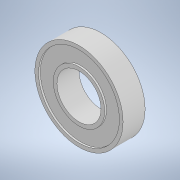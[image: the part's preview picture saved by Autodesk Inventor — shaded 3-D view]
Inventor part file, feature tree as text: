
AUTODESK INVENTOR PART (.ipt)
format: ipt  version: 2022 (Build 260153000, 153)  size: 133,632 bytes
history: native  units: mm
features: extrude x2, sketch x2, plane x1, mirror x1, projected_geometry x1
ambient origin geometry x8: Origin, YZ Plane, XZ Plane, XY Plane, X Axis, Y Axis, Z Axis, Center Point
bodies: Solid1 (feature_tree)
feature tree (7):
  extrude  "Extrusion1"  Depth=12.0mm
  extrude  "Extrusion2"  Depth=0.5mm
  plane  "Work Plane1"
  mirror  "Mirror1"
  sketch  "Sketch1"  dims[d0=12.0mm d1=24.0mm]
  sketch  "Sketch2"  dims[d2=6.0mm d3=0.0mm d4=1.0mm d5=1.0mm d6=0.5mm d7=0.0mm]
  projected_geometry  "Projected Loop1"
